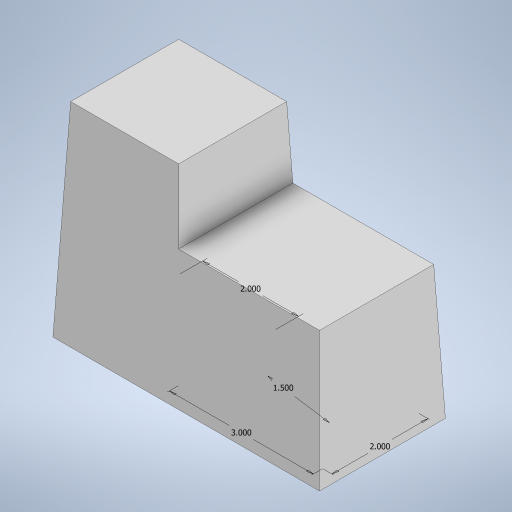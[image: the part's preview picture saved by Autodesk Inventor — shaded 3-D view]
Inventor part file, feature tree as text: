
AUTODESK INVENTOR PART (.ipt)
format: ipt  version: 2023 (Build 270158000, 158)  size: 214,528 bytes
history: native  units: in
note: dims shown in document units (in); Inventor stores cm internally (conversion verified against a paired STEP export)
features: extrude x2, sketch x1, thicken_offset x1, draft x1
ambient origin geometry x8: Origin, YZ Plane, XZ Plane, XY Plane, X Axis, Y Axis, Z Axis, Center Point
bodies: Solid1 (feature_tree)
feature tree (5):
  sketch  "Sketch1"  dims[d0=3.0in d1=2.0in d2=2.0in d3=1.5in d4=2.528in d5=0.0in d6=4.0in d7=0.0in d8=0.125in d9=0.125in d10=0.0172in]
  extrude  "Extrusion1"  Depth=2.0in
  extrude  "Extrusion2"  Depth=2.0in
  thicken_offset  "Thicken1"
  draft  "FaceDraft1"
